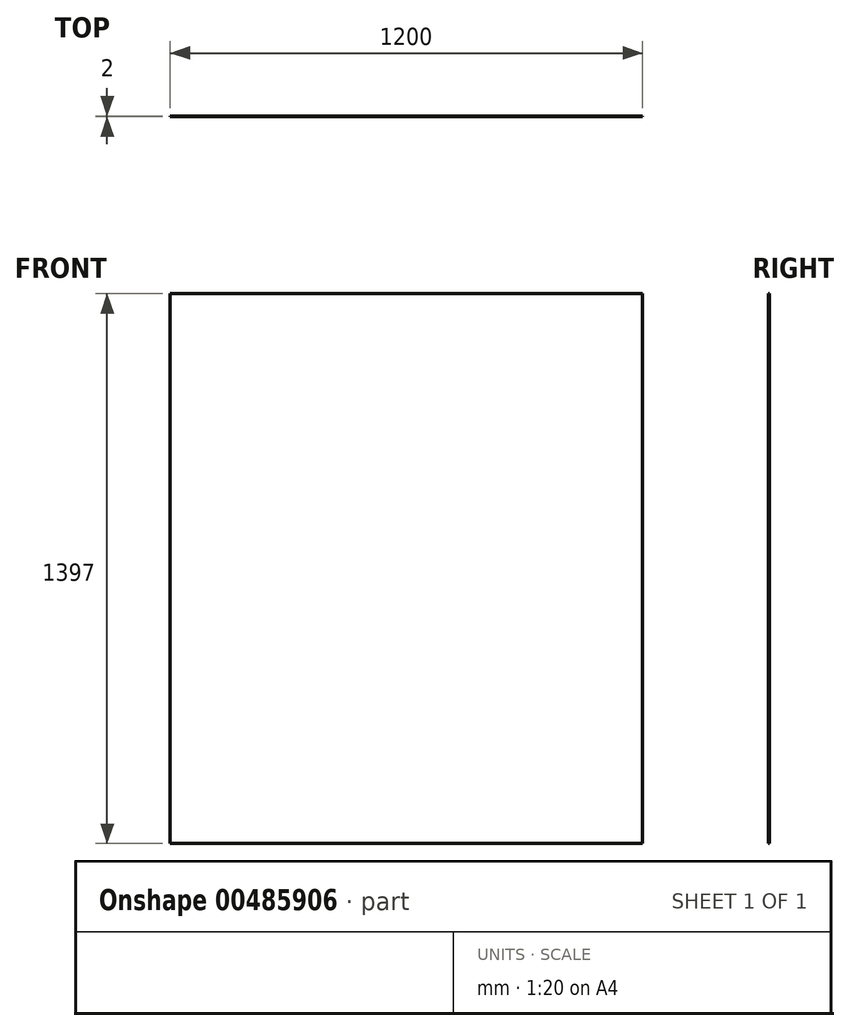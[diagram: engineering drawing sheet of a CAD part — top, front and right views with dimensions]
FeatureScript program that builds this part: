
annotation { "Feature Type Name" : "Feature", "Feature Type Description" : "" }
export const myFeature = defineFeature(function(context is Context, id is Id, definition is map)
    precondition{}
    {
        {
            var Q0;
            Q0=qCreatedBy(makeId("Front.planeOp"),FACE);
            var sketch = newSketch(context, id + "F0", { "sketchPlane" : qUnion([Q0])});
            skLineSegment(sketch, "E0.bottom", {"start": v(600, -698.5) * mm, "end": v(-600, -698.5) * mm});
            skLineSegment(sketch, "E0.top", {"start": v(600, 698.5) * mm, "end": v(-600, 698.5) * mm});
            skLineSegment(sketch, "E0.left", {"start": v(600, -698.5) * mm, "end": v(600, 698.5) * mm});
            skLineSegment(sketch, "E0.right", {"start": v(-600, -698.5) * mm, "end": v(-600, 698.5) * mm});
            skPoint(sketch, "E0.middle", {"position": v(0, 0) * mm});
            skSolve(sketch);
        }
        {
            var Q0;
            Q0=qSketchRegion(id+"F0",true);
            extrude(context, id + "F1", {"entities" : qUnion([Q0]), "depth" : 2 * mm});
        }
    });
